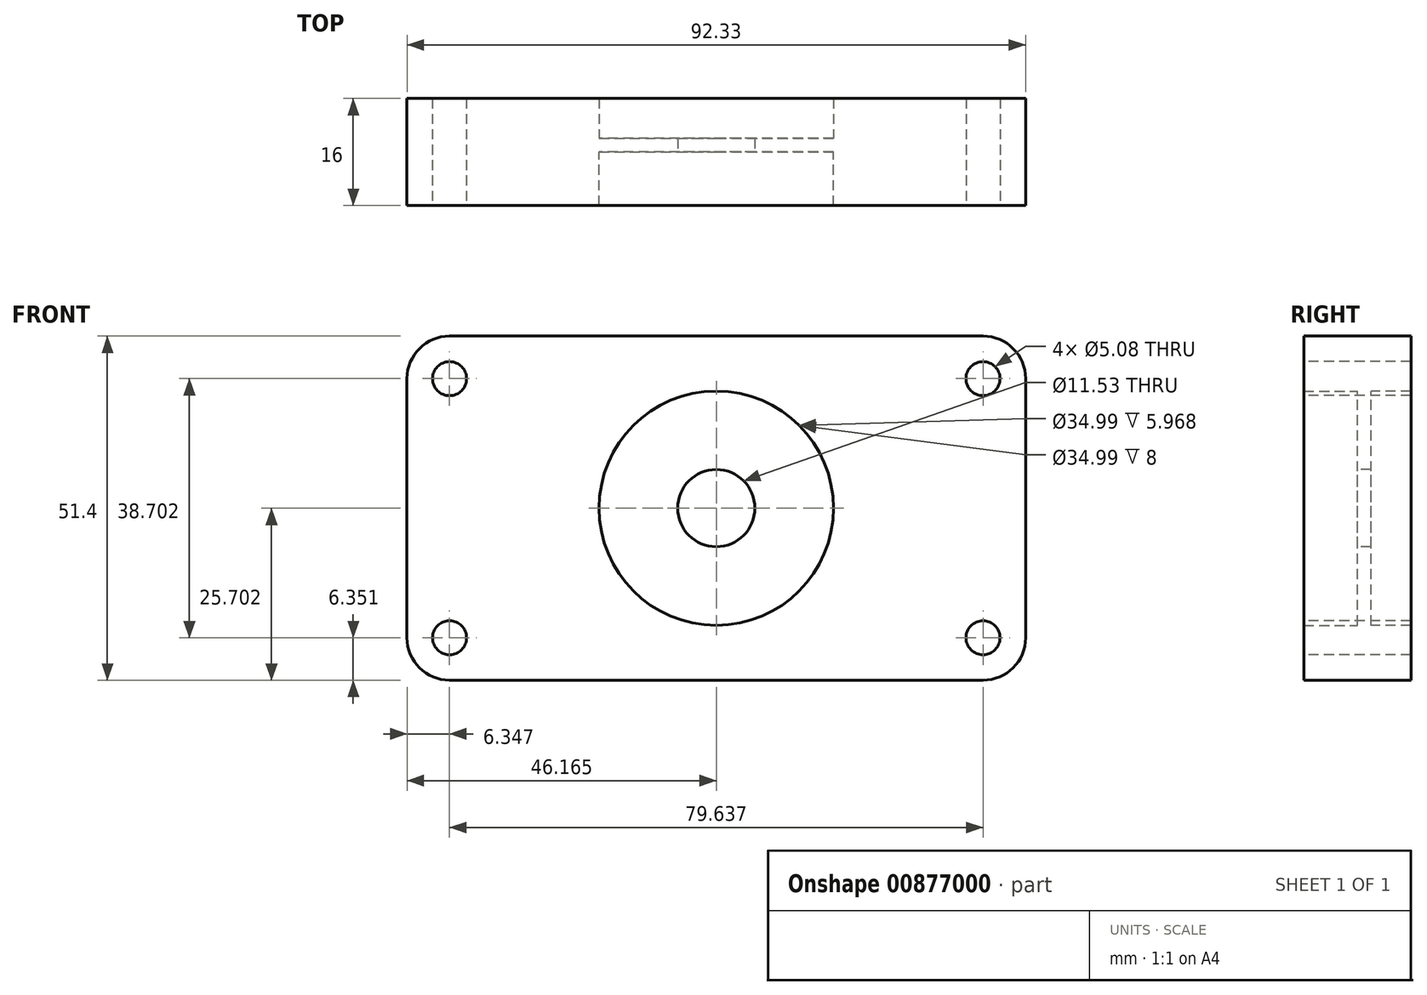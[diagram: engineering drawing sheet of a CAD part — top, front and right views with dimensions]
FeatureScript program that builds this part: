
annotation { "Feature Type Name" : "Feature", "Feature Type Description" : "" }
export const myFeature = defineFeature(function(context is Context, id is Id, definition is map)
    precondition{}
    {
        {
            var Q0;
            Q0=qCreatedBy(makeId("Front.planeOp"),FACE);
            var sketch = newSketch(context, id + "F0", { "sketchPlane" : qUnion([Q0])});
            skLineSegment(sketch, "E0.bottom", {"start": v(-36.63, -25.73) * mm, "end": v(43, -25.73) * mm});
            skLineSegment(sketch, "E0.top", {"start": v(-36.63, 25.67) * mm, "end": v(43, 25.67) * mm});
            skLineSegment(sketch, "E0.left", {"start": v(-42.98, -19.38) * mm, "end": v(-42.98, 19.32) * mm});
            skLineSegment(sketch, "E0.right", {"start": v(49.35, -19.38) * mm, "end": v(49.35, 19.32) * mm});
            skArc(sketch, "E1.filletArc", {"start": v(-36.63, 25.67) * mm, "mid": v(-41.12, 23.81) * mm, "end": v(-42.98, 19.32) * mm});
            skArc(sketch, "E2.filletArc", {"start": v(49.35, 19.32) * mm, "mid": v(47.5, 23.81) * mm, "end": v(43, 25.67) * mm});
            skArc(sketch, "E3.filletArc", {"start": v(43, -25.73) * mm, "mid": v(47.5, -23.87) * mm, "end": v(49.35, -19.38) * mm});
            skArc(sketch, "E4.filletArc", {"start": v(-42.98, -19.38) * mm, "mid": v(-41.12, -23.87) * mm, "end": v(-36.63, -25.73) * mm});
            skLineSegment(sketch, "E5.bottom", {"start": v(-36.63, -19.38) * mm, "end": v(-36.63, -19.38) * mm});
            skLineSegment(sketch, "E6", {"start": v(-29.17, 11.02) * mm, "end": v(-29.17, -10.38) * mm});
            skLineSegment(sketch, "E7", {"start": v(35.54, -10.38) * mm, "end": v(35.54, 11.02) * mm});
            skCircle(sketch, "E8", {"center": v(3.19, -0.03) * mm, "radius": 17.5 * mm});
            skCircle(sketch, "E9", {"center": v(3.19, -0.03) * mm, "radius": 5.77 * mm});
            skCircle(sketch, "E10", {"center": v(3.19, -0.03) * mm, "radius": 11.85 * mm});
            skCircle(sketch, "E11", {"center": v(43, 19.32) * mm, "radius": 2.54 * mm});
            skCircle(sketch, "E12.MirrorC", {"center": v(-36.63, 19.32) * mm, "radius": 2.54 * mm});
            skCircle(sketch, "E13.MirrorC", {"center": v(43, -19.38) * mm, "radius": 2.54 * mm});
            skCircle(sketch, "E14.MirrorC", {"center": v(-36.63, -19.38) * mm, "radius": 2.54 * mm});
            skArc(sketch, "E15", {"start": v(-29.17, 11.68) * mm, "mid": v(-23.64, 13.72) * mm, "end": v(-22.17, 19.43) * mm});
            skArc(sketch, "E16.MirrorCS", {"start": v(-29.17, -11.73) * mm, "mid": v(-23.64, -13.78) * mm, "end": v(-22.17, -19.49) * mm});
            skArc(sketch, "E17.MirrorCS", {"start": v(35.54, 11.68) * mm, "mid": v(30, 13.72) * mm, "end": v(28.54, 19.43) * mm});
            skArc(sketch, "E18.MirrorCS", {"start": v(35.54, -11.73) * mm, "mid": v(30, -13.78) * mm, "end": v(28.54, -19.49) * mm});
            skLineSegment(sketch, "E19", {"start": v(-22.17, 19.43) * mm, "end": v(28.54, 19.43) * mm});
            skLineSegment(sketch, "E20", {"start": v(-22.17, -19.49) * mm, "end": v(28.54, -19.49) * mm});
            skSolve(sketch);
        }
        {
            var Q0;
            Q0=makeQuery(id+"F0.imprint","IMPRINT",FACE,{"disambiguationData":[TD([[makeQuery(id+"F0.imprint","IMPRINT",EDGE,{"derivedFrom":sQuery(id+"F0.wireOp",EDGE,"E9")}),-1.0]])]});
            var Q1;
            Q1=makeQuery(id+"F0.imprint","IMPRINT",FACE,{"disambiguationData":[TD([[makeQuery(id+"F0.imprint","IMPRINT",EDGE,{"derivedFrom":sQuery(id+"F0.wireOp",EDGE,"E8")}),1.0]])]});
            extrude(context, id + "F1", {"entities" : qUnion([Q0, Q1]), "oppositeDirection" : true, "depth" : 2.03 * mm, "offsetDistance" : 25.4 * mm});
        }
        {
            var Q0;
            Q0 = qSketchRegion(id + "F0", true);
            var Q1;
            Q1 = qSketchRegion(id + "Fer8EOLs38dmigR_0", true);
            extrude(context, id + "F2", {"entities" : qUnion([Q0, Q1]), "operationType" : NewBodyOperationType.ADD, "oppositeDirection" : true, "depth" : 8 * mm, "offsetDistance" : 25.4 * mm});
        }
        {
            var Q0;
            Q0 = qSketchRegion(id + "F0", true);
            extrude(context, id + "F3", {"entities" : qUnion([Q0]), "operationType" : NewBodyOperationType.ADD, "depth" : 8 * mm, "offsetDistance" : 25.4 * mm});
        }
    });
